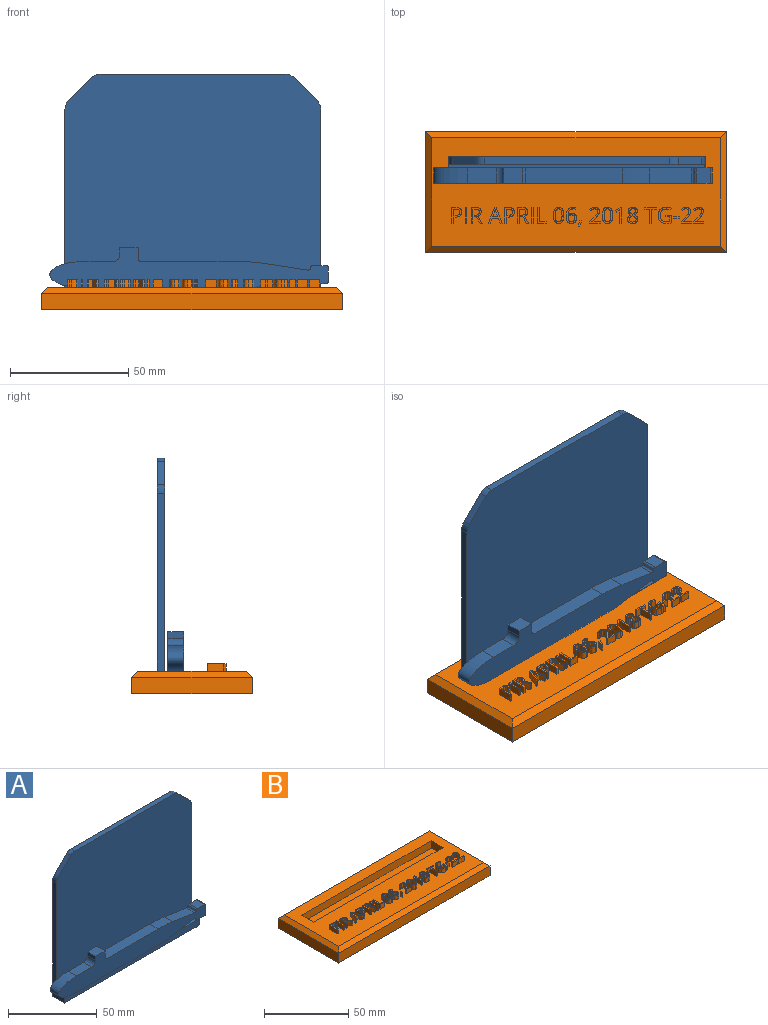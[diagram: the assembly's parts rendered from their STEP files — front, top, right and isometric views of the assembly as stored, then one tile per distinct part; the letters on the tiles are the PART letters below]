
ASSEMBLY  parts=2 mates=1
PART A: 43 faces, bbox 117.5x11x95.3 mm
  f0: plane 70.92x1.52mm, normal (0,0,-1), area 108.1mm2, adj f1,f13,f15,f32
  f1: plane 23.61x6.6mm, normal (0.15,0,-0.99), area 157.8mm2, adj f0,f14,f15,f18,f25
  f2: plane 6.6x0.11mm, normal (-1,0,0), area 0.7mm2, adj f14,f15,f18,f19
  f3: plane 6.6x5.84mm, normal (0,0,-1), area 38.6mm2, adj f14,f15,f19,f20
  f4: plane 6.6x5.84mm, normal (1,0,0), area 38.6mm2, adj f14,f15,f20,f21
  f5: plane 6.6x5.84mm, normal (0,0,1), area 38.6mm2, adj f14,f15,f21,f22
  f6: plane 6.6x0.11mm, normal (-1,0,0), area 0.7mm2, adj f14,f15,f22,f23
  f7: plane 17.86x6.6mm, normal (0.15,0,0.99), area 119.4mm2, adj f14,f15,f23,f24
  f8: plane 40.71x6.6mm, normal (0,0,1), area 268.9mm2, adj f14,f15,f17,f24
  f9: plane 6.6x4.36mm, normal (1,0,0), area 28.8mm2, adj f10,f14,f15,f17
  f10: plane 7.62x6.6mm, normal (0,0,1), area 50.3mm2, adj f9,f11,f14,f15
  f11: plane 6.6x2.84mm, normal (-1,0,0), area 18.7mm2, adj f10,f14,f15,f16
  f12: plane 12.19x6.6mm, normal (0,0,1), area 80.5mm2, adj f13,f14,f15,f16
  f13: extruded ~14.34x11.13mm, area 216.7mm2, adj f0,f12,f14,f15,f25
  f14: plane 117.52x17.01mm, normal (0,1,0), area 1199.5mm2, adj f1,f2,f3,f4,f5,f6,f7,f8
  f15: plane 117.52x17.01mm, normal (0,-1,0), area 1199.5mm2, adj f0,f1,f2,f3,f4,f5,f6,f7
  f16: cylinder r=3.05mm len=6.6mm, axis (0,1,0), area 31.6mm2, adj f11,f12,f14,f15
  f17: cylinder r=1.52mm len=6.6mm, axis (0,-1,0), area 15.8mm2, adj f8,f9,f14,f15
  f18: cylinder r=0.89mm len=6.6mm, axis (0,1,0), area 10.1mm2, adj f1,f2,f14,f15
  f19: cylinder r=0.89mm len=6.6mm, axis (0,-1,0), area 9.2mm2, adj f2,f3,f14,f15
  f20: cylinder r=0.89mm len=6.6mm, axis (0,1,0), area 9.2mm2, adj f3,f4,f14,f15
  f21: cylinder r=0.89mm len=6.6mm, axis (0,-1,0), area 9.2mm2, adj f4,f5,f14,f15
  f22: cylinder r=0.89mm len=6.6mm, axis (0,1,0), area 9.2mm2, adj f5,f6,f14,f15
  f23: cylinder r=0.89mm len=6.6mm, axis (0,-1,0), area 10.1mm2, adj f6,f7,f14,f15
  f24: cylinder r=76.2mm len=11.57mm, axis (0,-1,0), area 76.7mm2, adj f7,f8,f14,f15
  f25: plane 107.95x6.35mm, normal (0,0,1), area 325.2mm2, adj f1,f13,f14,f26,f27,f29,f32
  f26: plane 107.95x90.17mm, normal (0,-1,0), area 9570.3mm2, adj f25,f27,f29,f30,f33,f34,f35,f36
  f27: plane 79.68x9.53mm, normal (-1,0,0), area 280.4mm2, adj f25,f26,f31,f32,f35,f40
  f28: plane 106.43x8mm, normal (0,0,-1), area 851.5mm2, adj f39,f40,f41,f42
  f29: plane 79.68x9.53mm, normal (1,0,0), area 280.4mm2, adj f25,f26,f31,f32,f36,f41
  f30: plane 78.34x3.18mm, normal (0,0,1), area 248.7mm2, adj f26,f31,f37,f38
  f31: plane 107.95x94.49mm, normal (0,1,0), area 10036.5mm2, adj f27,f29,f30,f33,f34,f35,f36,f37
  f32: plane 107.95x4.32mm, normal (0,-1,0), area 466.1mm2, adj f0,f25,f27,f29,f42
  f33: plane 9.72x9.72mm, normal (0.71,0,0.71), area 43.7mm2, adj f26,f31,f36,f37
  f34: plane 9.72x9.72mm, normal (-0.71,0,0.71), area 43.7mm2, adj f26,f31,f35,f38
  f35: cylinder r=5.08mm len=3.59mm, axis (0,-1,0), area 12.7mm2, adj f26,f27,f31,f34
  f36: cylinder r=5.08mm len=3.59mm, axis (0,1,0), area 12.7mm2, adj f26,f29,f31,f33
  f37: cylinder r=5.08mm len=3.59mm, axis (0,1,0), area 12.7mm2, adj f26,f30,f31,f33
  f38: cylinder r=5.08mm len=3.59mm, axis (0,1,0), area 12.7mm2, adj f26,f30,f31,f34
  f39: plane 107.95x0.76mm, normal (0,0.71,-0.71), area 115.5mm2, adj f28,f31,f40,f41
  f40: plane 9.53x0.76mm, normal (-0.71,0,-0.71), area 9.4mm2, adj f27,f28,f39,f42
  f41: plane 9.53x0.76mm, normal (0.71,0,-0.71), area 9.4mm2, adj f28,f29,f39,f42
  f42: plane 107.95x0.76mm, normal (0,-0.71,-0.71), area 115.5mm2, adj f28,f32,f40,f41
PART B: 334 faces, bbox 127x50.8x12.7 mm
  f0: plane 121.92x45.72mm, normal (0,0,1), area 4230.8mm2, adj f6,f7,f8,f9,f16,f17,f18,f19
  f1: plane 50.8x6.99mm, normal (-1,0,0), area 354.8mm2, adj f2,f4,f5,f9
  f2: plane 127x50.8mm, normal (0,0,-1), area 6451.6mm2, adj f1,f3,f4,f5
  f3: plane 50.8x6.99mm, normal (1,0,0), area 354.8mm2, adj f2,f4,f5,f6
  f4: plane 127x6.99mm, normal (0,-1,0), area 887.1mm2, adj f1,f2,f3,f7
  f5: plane 127x6.99mm, normal (0,1,0), area 887.1mm2, adj f1,f2,f3,f8
  f6: plane 50.8x2.54mm, normal (0.71,0,0.71), area 173.4mm2, adj f0,f3,f7,f8
  f7: plane 127x2.54mm, normal (0,-0.71,0.71), area 447.1mm2, adj f0,f4,f6,f9
  f8: plane 127x2.54mm, normal (0,0.71,0.71), area 447.1mm2, adj f0,f5,f6,f9
  f9: plane 50.8x2.54mm, normal (-0.71,0,0.71), area 173.4mm2, adj f0,f1,f7,f8
  f10: plane 3.18x0.7mm, normal (0,1,0), area 2.2mm2, adj f11,f24,f25,f26
  f11: plane 3.18x2.69mm, normal (1,0,0), area 8.6mm2, adj f10,f12,f25,f26
  f12: plane 3.18x0.86mm, normal (0,-1,0), area 2.7mm2, adj f11,f13,f25,f26
  f13: extruded ~3.18x1.34mm, area 4.5mm2, adj f12,f14,f25,f26
  f14: extruded ~3.18x0.98mm, area 3.5mm2, adj f13,f15,f25,f26
  f15: extruded ~3.18x1.06mm, area 3.8mm2, adj f14,f24,f25,f26
  f16: extruded ~3.18x1.55mm, area 5.6mm2, adj f0,f17,f23,f25
  f17: extruded ~3.18x2.48mm, area 11.4mm2, adj f0,f16,f18,f25
  f18: plane 3.18x1.72mm, normal (0,1,0), area 5.5mm2, adj f0,f17,f19,f25
  f19: plane 6.63x3.18mm, normal (-1,0,0), area 21.1mm2, adj f0,f18,f20,f25
  f20: plane 3.18x0.77mm, normal (0,-1,0), area 2.4mm2, adj f0,f19,f21,f25
  f21: plane 3.18x2.61mm, normal (1,0,0), area 8.3mm2, adj f0,f20,f22,f25
  f22: plane 3.18x0.78mm, normal (0,-1,0), area 2.5mm2, adj f0,f21,f23,f25
  f23: extruded ~3.18x1.97mm, area 6.6mm2, adj f0,f16,f22,f25
  f24: extruded ~3.18x1.48mm, area 4.9mm2, adj f10,f15,f25,f26
  f25: plane 6.63x4.2mm, normal (0,0,1), area 10.8mm2, adj f10,f11,f12,f13,f14,f15,f16,f17
  f26: plane 2.69x2.64mm, normal (0,0,1), area 6.3mm2, adj f10,f11,f12,f13,f14,f15,f24
  f27: plane 6.63x3.18mm, normal (-1,0,0), area 21.1mm2, adj f0,f28,f30,f31
  f28: plane 3.18x0.77mm, normal (0,-1,0), area 2.4mm2, adj f0,f27,f29,f31
  f29: plane 6.63x3.18mm, normal (1,0,0), area 21.1mm2, adj f0,f28,f30,f31
  f30: plane 3.18x0.77mm, normal (0,1,0), area 2.4mm2, adj f0,f27,f29,f31
  f31: plane 6.63x0.77mm, normal (0,0,1), area 5.1mm2, adj f27,f28,f29,f30
  f32: plane 3.18x1.06mm, normal (0,1,0), area 3.4mm2, adj f33,f49,f50,f51
  f33: plane 3.18x2.54mm, normal (1,0,0), area 8mm2, adj f32,f34,f50,f51
  f34: plane 3.18x1mm, normal (0,-1,0), area 3.2mm2, adj f33,f35,f50,f51
  f35: extruded ~3.18x1.25mm, area 4.1mm2, adj f34,f36,f50,f51
  f36: extruded ~3.18x0.95mm, area 3.4mm2, adj f35,f37,f50,f51
  f37: extruded ~3.18x0.97mm, area 3.4mm2, adj f36,f49,f50,f51
  f38: plane 3.18x2.76mm, normal (1,0,0), area 8.8mm2, adj f0,f39,f48,f50
  f39: plane 3.18x1.38mm, normal (0,-1,0), area 4.4mm2, adj f0,f38,f40,f50
  f40: plane 3.18x2.76mm, normal (-0.86,-0.5,0), area 10.1mm2, adj f0,f39,f41,f50
  f41: plane 3.18x0.91mm, normal (0,-1,0), area 2.9mm2, adj f0,f40,f42,f50
  f42: plane 3.18x2.98mm, normal (0.86,0.52,0), area 11.1mm2, adj f0,f41,f43,f50
  f43: extruded ~3.18x1.78mm, area 7.6mm2, adj f0,f42,f44,f50
  f44: extruded ~3.18x1.41mm, area 5mm2, adj f0,f43,f45,f50
  f45: extruded ~3.18x1.8mm, area 6mm2, adj f0,f44,f46,f50
  f46: plane 3.18x1.82mm, normal (0,1,0), area 5.8mm2, adj f0,f45,f47,f50
  f47: plane 6.63x3.18mm, normal (-1,0,0), area 21.1mm2, adj f0,f46,f48,f50
  f48: plane 3.18x0.77mm, normal (0,-1,0), area 2.4mm2, adj f0,f38,f47,f50
  f49: extruded ~3.18x1.2mm, area 4mm2, adj f32,f37,f50,f51
  f50: plane 6.63x4.67mm, normal (0,0,1), area 13.2mm2, adj f32,f33,f34,f35,f36,f37,f38,f39
  f51: plane 2.64x2.54mm, normal (0,0,1), area 6mm2, adj f32,f33,f34,f35,f36,f37,f49
  f52: plane 3.18x2.06mm, normal (-0.94,-0.35,0), area 7mm2, adj f53,f64,f65,f66
  f53: plane 3.18x2.15mm, normal (0,1,0), area 6.8mm2, adj f52,f54,f65,f66
  f54: plane 3.18x2.06mm, normal (0.94,-0.35,0), area 7mm2, adj f53,f55,f65,f66
  f55: extruded ~3.18x0.96mm, area 3.2mm2, adj f54,f64,f65,f66
  f56: plane 3.18x2.11mm, normal (-0.93,-0.36,0), area 7.2mm2, adj f0,f57,f63,f65
  f57: plane 3.18x0.8mm, normal (0,-1,0), area 2.5mm2, adj f0,f56,f58,f65
  f58: plane 6.66x3.18mm, normal (0.93,0.36,0), area 22.7mm2, adj f0,f57,f59,f65
  f59: plane 3.18x0.65mm, normal (0,1,0), area 2.1mm2, adj f0,f58,f60,f65
  f60: plane 6.66x3.18mm, normal (-0.93,0.37,0), area 22.7mm2, adj f0,f59,f61,f65
  f61: plane 3.18x0.78mm, normal (0,-1,0), area 2.5mm2, adj f0,f60,f62,f65
  f62: plane 3.18x2.11mm, normal (0.93,-0.36,0), area 7.2mm2, adj f0,f61,f63,f65
  f63: plane 3.18x2.66mm, normal (0,-1,0), area 8.4mm2, adj f0,f56,f62,f65
  f64: extruded ~3.18x0.96mm, area 3.2mm2, adj f52,f55,f65,f66
  f65: plane 6.66x5.88mm, normal (0,0,1), area 11.3mm2, adj f52,f53,f54,f55,f56,f57,f58,f59
  f66: plane 3.01x2.15mm, normal (0,0,1), area 3.1mm2, adj f52,f53,f54,f55,f64
  f67: plane 3.18x0.7mm, normal (0,1,0), area 2.2mm2, adj f68,f81,f82,f83
  f68: plane 3.18x2.69mm, normal (1,0,0), area 8.6mm2, adj f67,f69,f82,f83
  f69: plane 3.18x0.86mm, normal (0,-1,0), area 2.7mm2, adj f68,f70,f82,f83
  f70: extruded ~3.18x1.34mm, area 4.5mm2, adj f69,f71,f82,f83
  f71: extruded ~3.18x0.98mm, area 3.5mm2, adj f70,f72,f82,f83
  f72: extruded ~3.18x1.06mm, area 3.8mm2, adj f71,f81,f82,f83
  f73: extruded ~3.18x1.55mm, area 5.6mm2, adj f0,f74,f80,f82
  f74: extruded ~3.18x2.48mm, area 11.4mm2, adj f0,f73,f75,f82
  f75: plane 3.18x1.72mm, normal (0,1,0), area 5.5mm2, adj f0,f74,f76,f82
  f76: plane 6.63x3.18mm, normal (-1,0,0), area 21.1mm2, adj f0,f75,f77,f82
  f77: plane 3.18x0.77mm, normal (0,-1,0), area 2.4mm2, adj f0,f76,f78,f82
  f78: plane 3.18x2.61mm, normal (1,0,0), area 8.3mm2, adj f0,f77,f79,f82
  f79: plane 3.18x0.78mm, normal (0,-1,0), area 2.5mm2, adj f0,f78,f80,f82
  f80: extruded ~3.18x1.97mm, area 6.6mm2, adj f0,f73,f79,f82
  f81: extruded ~3.18x1.48mm, area 4.9mm2, adj f67,f72,f82,f83
  f82: plane 6.63x4.2mm, normal (0,0,1), area 10.8mm2, adj f67,f68,f69,f70,f71,f72,f73,f74
  f83: plane 2.69x2.64mm, normal (0,0,1), area 6.3mm2, adj f67,f68,f69,f70,f71,f72,f81
  f84: plane 3.18x1.06mm, normal (0,1,0), area 3.4mm2, adj f85,f101,f102,f103
  f85: plane 3.18x2.54mm, normal (1,0,0), area 8mm2, adj f84,f86,f102,f103
  f86: plane 3.18x1mm, normal (0,-1,0), area 3.2mm2, adj f85,f87,f102,f103
  f87: extruded ~3.18x1.25mm, area 4.1mm2, adj f86,f88,f102,f103
  f88: extruded ~3.18x0.95mm, area 3.4mm2, adj f87,f89,f102,f103
  f89: extruded ~3.18x0.97mm, area 3.4mm2, adj f88,f101,f102,f103
  f90: plane 3.18x2.76mm, normal (1,0,0), area 8.8mm2, adj f0,f91,f100,f102
  f91: plane 3.18x1.38mm, normal (0,-1,0), area 4.4mm2, adj f0,f90,f92,f102
  f92: plane 3.18x2.76mm, normal (-0.86,-0.5,0), area 10.1mm2, adj f0,f91,f93,f102
  f93: plane 3.18x0.91mm, normal (0,-1,0), area 2.9mm2, adj f0,f92,f94,f102
  f94: plane 3.18x2.98mm, normal (0.86,0.52,0), area 11.1mm2, adj f0,f93,f95,f102
  f95: extruded ~3.18x1.78mm, area 7.6mm2, adj f0,f94,f96,f102
  f96: extruded ~3.18x1.41mm, area 5mm2, adj f0,f95,f97,f102
  f97: extruded ~3.18x1.8mm, area 6mm2, adj f0,f96,f98,f102
  f98: plane 3.18x1.82mm, normal (0,1,0), area 5.8mm2, adj f0,f97,f99,f102
  f99: plane 6.63x3.18mm, normal (-1,0,0), area 21.1mm2, adj f0,f98,f100,f102
  f100: plane 3.18x0.77mm, normal (0,-1,0), area 2.4mm2, adj f0,f90,f99,f102
  f101: extruded ~3.18x1.2mm, area 4mm2, adj f84,f89,f102,f103
  f102: plane 6.63x4.67mm, normal (0,0,1), area 13.2mm2, adj f84,f85,f86,f87,f88,f89,f90,f91
  f103: plane 2.64x2.54mm, normal (0,0,1), area 6mm2, adj f84,f85,f86,f87,f88,f89,f101
  f104: plane 6.63x3.18mm, normal (-1,0,0), area 21.1mm2, adj f0,f105,f107,f108
  f105: plane 3.18x0.77mm, normal (0,-1,0), area 2.4mm2, adj f0,f104,f106,f108
  f106: plane 6.63x3.18mm, normal (1,0,0), area 21.1mm2, adj f0,f105,f107,f108
  f107: plane 3.18x0.77mm, normal (0,1,0), area 2.4mm2, adj f0,f104,f106,f108
  f108: plane 6.63x0.77mm, normal (0,0,1), area 5.1mm2, adj f104,f105,f106,f107
  f109: plane 6.63x3.18mm, normal (-1,0,0), area 21.1mm2, adj f0,f110,f114,f115
  f110: plane 3.7x3.18mm, normal (0,-1,0), area 11.7mm2, adj f0,f109,f111,f115
  f111: plane 3.18x0.7mm, normal (1,0,0), area 2.2mm2, adj f0,f110,f112,f115
  f112: plane 3.18x2.93mm, normal (0,1,0), area 9.3mm2, adj f0,f111,f113,f115
  f113: plane 5.93x3.18mm, normal (1,0,0), area 18.8mm2, adj f0,f112,f114,f115
  f114: plane 3.18x0.77mm, normal (0,1,0), area 2.4mm2, adj f0,f109,f113,f115
  f115: plane 6.63x3.7mm, normal (0,0,1), area 7.2mm2, adj f109,f110,f111,f112,f113,f114
  f116: extruded ~3.18x2.11mm, area 6.8mm2, adj f117,f131,f132,f133
  f117: extruded ~3.18x2.1mm, area 6.8mm2, adj f116,f118,f132,f133
  f118: extruded ~3.18x1.08mm, area 4.3mm2, adj f117,f119,f132,f133
  f119: extruded ~3.18x1.09mm, area 4.3mm2, adj f118,f120,f132,f133
  f120: extruded ~3.18x2.09mm, area 6.8mm2, adj f119,f121,f132,f133
  f121: extruded ~3.18x2.1mm, area 6.8mm2, adj f120,f122,f132,f133
  f122: extruded ~3.18x1.09mm, area 4.3mm2, adj f121,f131,f132,f133
  f123: extruded ~3.18x2.57mm, area 8.4mm2, adj f0,f124,f130,f132
  f124: extruded ~3.18x2.53mm, area 8.3mm2, adj f0,f123,f125,f132
  f125: extruded ~3.18x1.64mm, area 6.2mm2, adj f0,f124,f126,f132
  f126: extruded ~3.18x1.65mm, area 6.1mm2, adj f0,f125,f127,f132
  f127: extruded ~3.18x2.57mm, area 8.4mm2, adj f0,f126,f128,f132
  f128: extruded ~3.18x2.55mm, area 8.4mm2, adj f0,f127,f129,f132
  f129: extruded ~3.18x1.63mm, area 6.1mm2, adj f0,f128,f130,f132
  f130: extruded ~3.18x1.66mm, area 6.2mm2, adj f0,f123,f129,f132
  f131: extruded ~3.18x1.08mm, area 4.3mm2, adj f116,f122,f132,f133
  f132: plane 6.83x4.39mm, normal (0,0,1), area 11.6mm2, adj f116,f117,f118,f119,f120,f121,f122,f123
  f133: plane 5.53x2.85mm, normal (0,0,1), area 13.3mm2, adj f116,f117,f118,f119,f120,f121,f122,f131
  f134: extruded ~3.18x1mm, area 3.5mm2, adj f135,f158,f159,f160
  f135: extruded ~3.18x0.76mm, area 2.6mm2, adj f134,f136,f159,f160
  f136: extruded ~3.18x0.64mm, area 2.6mm2, adj f135,f137,f159,f160
  f137: extruded ~3.18x0.87mm, area 2.8mm2, adj f136,f138,f159,f160
  f138: extruded ~3.18x0.61mm, area 2.1mm2, adj f137,f139,f159,f160
  f139: extruded ~3.18x0.54mm, area 2.3mm2, adj f138,f140,f159,f160
  f140: extruded ~3.18x0.75mm, area 2.5mm2, adj f139,f141,f159,f160
  f141: extruded ~3.18x0.99mm, area 3.5mm2, adj f140,f142,f159,f160
  f142: extruded ~3.18x1.03mm, area 3.5mm2, adj f141,f158,f159,f160
  f143: extruded ~3.18x2.92mm, area 9.8mm2, adj f0,f144,f157,f159
  f144: extruded ~3.18x2.15mm, area 7.2mm2, adj f0,f143,f145,f159
  f145: extruded ~3.18x1.63mm, area 6mm2, adj f0,f144,f146,f159
  f146: extruded ~3.18x1.53mm, area 5.4mm2, adj f0,f145,f147,f159
  f147: extruded ~3.18x1.63mm, area 5.6mm2, adj f0,f146,f148,f159
  f148: extruded ~3.18x1.46mm, area 5.1mm2, adj f0,f147,f149,f159
  f149: extruded ~3.18x1.41mm, area 4.9mm2, adj f0,f148,f150,f159
  f150: extruded ~3.18x1.58mm, area 5.9mm2, adj f0,f149,f151,f159
  f151: plane 3.18x0.05mm, normal (0,1,0), area 0.2mm2, adj f0,f150,f152,f159
  f152: extruded ~3.18x2.09mm, area 7mm2, adj f0,f151,f153,f159
  f153: extruded ~3.18x1.63mm, area 5.8mm2, adj f0,f152,f154,f159
  f154: extruded ~3.18x0.8mm, area 2.6mm2, adj f0,f153,f155,f159
  f155: plane 3.18x0.65mm, normal (1,0,0), area 2.1mm2, adj f0,f154,f156,f159
  f156: extruded ~3.18x0.81mm, area 2.6mm2, adj f0,f155,f157,f159
  f157: extruded ~3.18x2.25mm, area 8.1mm2, adj f0,f143,f156,f159
  f158: extruded ~3.18x1.17mm, area 4mm2, adj f134,f142,f159,f160
  f159: plane 6.82x4.33mm, normal (0,0,1), area 11.4mm2, adj f134,f135,f136,f137,f138,f139,f140,f141
  f160: plane 2.99x2.81mm, normal (0,0,1), area 6.8mm2, adj f134,f135,f136,f137,f138,f139,f140,f141
  f161: plane 3.18x0.1mm, normal (0.84,0.55,0), area 0.4mm2, adj f0,f162,f167,f168
  f162: plane 3.18x0.83mm, normal (0,1,0), area 2.6mm2, adj f0,f161,f163,f168
  f163: extruded ~3.18x1.11mm, area 3.6mm2, adj f0,f162,f164,f168
  f164: extruded ~3.18x1.17mm, area 3.8mm2, adj f0,f163,f165,f168
  f165: plane 3.18x0.57mm, normal (0,-1,0), area 1.8mm2, adj f0,f164,f166,f168
  f166: extruded ~3.18x1.12mm, area 3.8mm2, adj f0,f165,f167,f168
  f167: extruded ~3.18x1.06mm, area 3.5mm2, adj f0,f161,f166,f168
  f168: plane 2.28x1.37mm, normal (0,0,1), area 1.7mm2, adj f161,f162,f163,f164,f165,f166,f167
  f169: plane 4.36x3.18mm, normal (0,-1,0), area 13.8mm2, adj f0,f170,f188,f189
  f170: plane 3.18x0.7mm, normal (1,0,0), area 2.2mm2, adj f0,f169,f171,f189
  f171: plane 3.41x3.18mm, normal (0,1,0), area 10.8mm2, adj f0,f170,f172,f189
  f172: plane 3.18x0.04mm, normal (1,0,0), area 0.1mm2, adj f0,f171,f173,f189
  f173: plane 3.18x1.45mm, normal (0.7,-0.71,0), area 6.4mm2, adj f0,f172,f174,f189
  f174: extruded ~3.18x1.56mm, area 6.5mm2, adj f0,f173,f175,f189
  f175: extruded ~3.18x1.25mm, area 4.2mm2, adj f0,f174,f176,f189
  f176: extruded ~3.18x1.29mm, area 4.6mm2, adj f0,f175,f177,f189
  f177: extruded ~3.18x1.47mm, area 5mm2, adj f0,f176,f178,f189
  f178: extruded ~3.18x2mm, area 6.9mm2, adj f0,f177,f179,f189
  f179: plane 3.18x0.51mm, normal (-0.79,-0.61,0), area 2.1mm2, adj f0,f178,f180,f189
  f180: extruded ~3.18x0.82mm, area 3.1mm2, adj f0,f179,f181,f189
  f181: extruded ~3.18x0.78mm, area 2.5mm2, adj f0,f180,f182,f189
  f182: extruded ~3.18x0.89mm, area 3.1mm2, adj f0,f181,f183,f189
  f183: extruded ~3.18x0.84mm, area 2.9mm2, adj f0,f182,f184,f189
  f184: extruded ~3.18x0.7mm, area 2.3mm2, adj f0,f183,f185,f189
  f185: extruded ~3.18x0.67mm, area 2.5mm2, adj f0,f184,f186,f189
  f186: extruded ~3.18x1.15mm, area 5mm2, adj f0,f185,f187,f189
  f187: plane 3.18x1.75mm, normal (-0.71,0.71,0), area 7.9mm2, adj f0,f186,f188,f189
  f188: plane 3.18x0.65mm, normal (-1,0,0), area 2.1mm2, adj f0,f169,f187,f189
  f189: plane 6.73x4.36mm, normal (0,0,1), area 9.7mm2, adj f169,f170,f171,f172,f173,f174,f175,f176
  f190: extruded ~3.18x2.11mm, area 6.8mm2, adj f191,f205,f206,f207
  f191: extruded ~3.18x2.1mm, area 6.8mm2, adj f190,f192,f206,f207
  f192: extruded ~3.18x1.08mm, area 4.3mm2, adj f191,f193,f206,f207
  f193: extruded ~3.18x1.09mm, area 4.3mm2, adj f192,f194,f206,f207
  f194: extruded ~3.18x2.09mm, area 6.8mm2, adj f193,f195,f206,f207
  f195: extruded ~3.18x2.1mm, area 6.8mm2, adj f194,f196,f206,f207
  f196: extruded ~3.18x1.09mm, area 4.3mm2, adj f195,f205,f206,f207
  f197: extruded ~3.18x2.57mm, area 8.4mm2, adj f0,f198,f204,f206
  f198: extruded ~3.18x2.53mm, area 8.3mm2, adj f0,f197,f199,f206
  f199: extruded ~3.18x1.64mm, area 6.2mm2, adj f0,f198,f200,f206
  f200: extruded ~3.18x1.65mm, area 6.1mm2, adj f0,f199,f201,f206
  f201: extruded ~3.18x2.57mm, area 8.4mm2, adj f0,f200,f202,f206
  f202: extruded ~3.18x2.55mm, area 8.4mm2, adj f0,f201,f203,f206
  f203: extruded ~3.18x1.63mm, area 6.1mm2, adj f0,f202,f204,f206
  f204: extruded ~3.18x1.66mm, area 6.2mm2, adj f0,f197,f203,f206
  f205: extruded ~3.18x1.08mm, area 4.3mm2, adj f190,f196,f206,f207
  f206: plane 6.83x4.39mm, normal (0,0,1), area 11.6mm2, adj f190,f191,f192,f193,f194,f195,f196,f197
  f207: plane 5.53x2.85mm, normal (0,0,1), area 13.3mm2, adj f190,f191,f192,f193,f194,f195,f196,f205
  f208: plane 3.18x0.73mm, normal (0,-1,0), area 2.3mm2, adj f0,f209,f216,f217
  f209: plane 6.63x3.18mm, normal (1,0,0), area 21.1mm2, adj f0,f208,f210,f217
  f210: plane 3.18x0.63mm, normal (0,1,0), area 2mm2, adj f0,f209,f211,f217
  f211: plane 3.18x1.75mm, normal (-0.61,0.79,0), area 7mm2, adj f0,f210,f212,f217
  f212: plane 3.18x0.52mm, normal (-0.79,-0.61,0), area 2.1mm2, adj f0,f211,f213,f217
  f213: extruded ~3.18x1.08mm, area 4.4mm2, adj f0,f212,f214,f217
  f214: extruded ~3.18x0.21mm, area 0.9mm2, adj f0,f213,f215,f217
  f215: extruded ~3.18x1.12mm, area 3.5mm2, adj f0,f214,f216,f217
  f216: plane 4.73x3.18mm, normal (-1,0,0), area 15mm2, adj f0,f208,f215,f217
  f217: plane 6.63x2.39mm, normal (0,0,1), area 6mm2, adj f208,f209,f210,f211,f212,f213,f214,f215
  f218: extruded ~3.18x0.89mm, area 3mm2, adj f219,f248,f249,f250
  f219: extruded ~3.18x0.91mm, area 3.1mm2, adj f218,f220,f249,f250
  f220: extruded ~3.18x0.73mm, area 2.6mm2, adj f219,f221,f249,f250
  f221: extruded ~3.18x0.73mm, area 2.5mm2, adj f220,f222,f249,f250
  f222: extruded ~3.18x0.92mm, area 3.5mm2, adj f221,f223,f249,f250
  f223: extruded ~3.18x0.99mm, area 3.7mm2, adj f222,f224,f249,f250
  f224: extruded ~3.18x0.72mm, area 2.5mm2, adj f223,f248,f249,f250
  f225: extruded ~3.18x0.85mm, area 3.1mm2, adj f226,f246,f249,f251
  f226: extruded ~3.18x0.84mm, area 2.9mm2, adj f225,f227,f249,f251
  f227: extruded ~3.18x0.98mm, area 3.7mm2, adj f226,f228,f249,f251
  f228: extruded ~3.18x1.23mm, area 4.5mm2, adj f227,f229,f249,f251
  f229: extruded ~3.18x0.78mm, area 2.8mm2, adj f228,f230,f249,f251
  f230: extruded ~3.18x0.87mm, area 3.1mm2, adj f229,f231,f249,f251
  f231: extruded ~3.18x1.05mm, area 3.6mm2, adj f230,f246,f249,f251
  f232: extruded ~3.18x1.44mm, area 4.8mm2, adj f0,f233,f247,f249
  f233: extruded ~3.18x1.43mm, area 4.8mm2, adj f0,f232,f234,f249
  f234: extruded ~3.18x1.15mm, area 4.2mm2, adj f0,f233,f235,f249
  f235: extruded ~3.18x0.92mm, area 3.1mm2, adj f0,f234,f236,f249
  f236: extruded ~3.18x0.9mm, area 3.8mm2, adj f0,f235,f237,f249
  f237: extruded ~3.18x1.77mm, area 7.6mm2, adj f0,f236,f238,f249
  f238: extruded ~3.18x1.32mm, area 4.7mm2, adj f0,f237,f239,f249
  f239: extruded ~3.18x1.63mm, area 5.5mm2, adj f0,f238,f240,f249
  f240: extruded ~3.18x1.58mm, area 5.4mm2, adj f0,f239,f241,f249
  f241: extruded ~3.18x1.32mm, area 4.7mm2, adj f0,f240,f242,f249
  f242: extruded ~3.18x0.98mm, area 3.4mm2, adj f0,f241,f243,f249
  f243: extruded ~3.18x1.15mm, area 4.5mm2, adj f0,f242,f244,f249
  f244: extruded ~3.18x0.97mm, area 3.9mm2, adj f0,f243,f245,f249
  f245: extruded ~3.18x0.89mm, area 3.1mm2, adj f0,f244,f247,f249
  f246: extruded ~3.18x1.06mm, area 3.6mm2, adj f225,f231,f249,f251
  f247: extruded ~3.18x1.16mm, area 4.2mm2, adj f0,f232,f245,f249
  f248: extruded ~3.18x0.73mm, area 2.6mm2, adj f218,f224,f249,f250
  f249: plane 6.82x4.36mm, normal (0,0,1), area 13mm2, adj f218,f219,f220,f221,f222,f223,f224,f225
  f250: plane 2.45x2.31mm, normal (0,0,1), area 4.3mm2, adj f218,f219,f220,f221,f222,f223,f224,f248
  f251: plane 2.87x2.64mm, normal (0,0,1), area 5.8mm2, adj f225,f226,f227,f228,f229,f230,f231,f246
  f252: plane 3.18x0.77mm, normal (0,-1,0), area 2.4mm2, adj f0,f253,f259,f260
  f253: plane 5.95x3.18mm, normal (1,0,0), area 18.9mm2, adj f0,f252,f254,f260
  f254: plane 3.18x2.1mm, normal (0,-1,0), area 6.7mm2, adj f0,f253,f255,f260
  f255: plane 3.18x0.69mm, normal (1,0,0), area 2.2mm2, adj f0,f254,f256,f260
  f256: plane 4.97x3.18mm, normal (0,1,0), area 15.8mm2, adj f0,f255,f257,f260
  f257: plane 3.18x0.69mm, normal (-1,0,0), area 2.2mm2, adj f0,f256,f258,f260
  f258: plane 3.18x2.1mm, normal (0,-1,0), area 6.7mm2, adj f0,f257,f259,f260
  f259: plane 5.95x3.18mm, normal (-1,0,0), area 18.9mm2, adj f0,f252,f258,f260
  f260: plane 6.63x4.97mm, normal (0,0,1), area 8mm2, adj f252,f253,f254,f255,f256,f257,f258,f259
  f261: plane 3.18x2.25mm, normal (0,1,0), area 7.2mm2, adj f0,f262,f280,f281
  f262: plane 3.18x0.69mm, normal (-1,0,0), area 2.2mm2, adj f0,f261,f263,f281
  f263: plane 3.18x1.48mm, normal (0,-1,0), area 4.7mm2, adj f0,f262,f264,f281
  f264: plane 3.18x2.04mm, normal (-1,0,0), area 6.5mm2, adj f0,f263,f265,f281
  f265: extruded ~3.18x1.35mm, area 4.3mm2, adj f0,f264,f266,f281
  f266: extruded ~3.18x1.93mm, area 6.7mm2, adj f0,f265,f267,f281
  f267: extruded ~3.18x2.04mm, area 7mm2, adj f0,f266,f268,f281
  f268: extruded ~3.18x2mm, area 6.9mm2, adj f0,f267,f269,f281
  f269: extruded ~3.18x1.89mm, area 6.6mm2, adj f0,f268,f270,f281
  f270: extruded ~3.18x1.73mm, area 5.7mm2, adj f0,f269,f271,f281
  f271: plane 3.18x0.68mm, normal (0.92,-0.4,0), area 2.4mm2, adj f0,f270,f272,f281
  f272: extruded ~3.18x1.98mm, area 6.4mm2, adj f0,f271,f273,f281
  f273: extruded ~3.18x1.83mm, area 6mm2, adj f0,f272,f274,f281
  f274: extruded ~3.18x1.2mm, area 5.4mm2, adj f0,f273,f275,f281
  f275: extruded ~3.18x1.81mm, area 6mm2, adj f0,f274,f276,f281
  f276: extruded ~3.18x2.51mm, area 8.6mm2, adj f0,f275,f277,f281
  f277: extruded ~3.18x2.34mm, area 8.2mm2, adj f0,f276,f278,f281
  f278: extruded ~3.18x1.26mm, area 4mm2, adj f0,f277,f279,f281
  f279: extruded ~3.18x1.07mm, area 3.5mm2, adj f0,f278,f280,f281
  f280: plane 3.22x3.18mm, normal (1,0,0), area 10.2mm2, adj f0,f261,f279,f281
  f281: plane 6.82x5.52mm, normal (0,0,1), area 13.3mm2, adj f261,f262,f263,f264,f265,f266,f267,f268
  f282: plane 3.18x0.69mm, normal (-1,0,0), area 2.2mm2, adj f0,f283,f285,f286
  f283: plane 3.18x2.23mm, normal (0,-1,0), area 7.1mm2, adj f0,f282,f284,f286
  f284: plane 3.18x0.69mm, normal (1,0,0), area 2.2mm2, adj f0,f283,f285,f286
  f285: plane 3.18x2.23mm, normal (0,1,0), area 7.1mm2, adj f0,f282,f284,f286
  f286: plane 2.23x0.69mm, normal (0,0,1), area 1.5mm2, adj f282,f283,f284,f285
  f287: plane 4.36x3.18mm, normal (0,-1,0), area 13.8mm2, adj f0,f288,f306,f307
  f288: plane 3.18x0.7mm, normal (1,0,0), area 2.2mm2, adj f0,f287,f289,f307
  f289: plane 3.41x3.18mm, normal (0,1,0), area 10.8mm2, adj f0,f288,f290,f307
  f290: plane 3.18x0.04mm, normal (1,0,0), area 0.1mm2, adj f0,f289,f291,f307
  f291: plane 3.18x1.45mm, normal (0.7,-0.71,0), area 6.4mm2, adj f0,f290,f292,f307
  f292: extruded ~3.18x1.56mm, area 6.5mm2, adj f0,f291,f293,f307
  f293: extruded ~3.18x1.25mm, area 4.2mm2, adj f0,f292,f294,f307
  f294: extruded ~3.18x1.29mm, area 4.6mm2, adj f0,f293,f295,f307
  f295: extruded ~3.18x1.47mm, area 5mm2, adj f0,f294,f296,f307
  f296: extruded ~3.18x2mm, area 6.9mm2, adj f0,f295,f297,f307
  f297: plane 3.18x0.51mm, normal (-0.79,-0.61,0), area 2.1mm2, adj f0,f296,f298,f307
  f298: extruded ~3.18x0.82mm, area 3.1mm2, adj f0,f297,f299,f307
  f299: extruded ~3.18x0.78mm, area 2.5mm2, adj f0,f298,f300,f307
  f300: extruded ~3.18x0.89mm, area 3.1mm2, adj f0,f299,f301,f307
  f301: extruded ~3.18x0.84mm, area 2.9mm2, adj f0,f300,f302,f307
  f302: extruded ~3.18x0.7mm, area 2.3mm2, adj f0,f301,f303,f307
  f303: extruded ~3.18x0.67mm, area 2.5mm2, adj f0,f302,f304,f307
  f304: extruded ~3.18x1.15mm, area 5mm2, adj f0,f303,f305,f307
  f305: plane 3.18x1.75mm, normal (-0.71,0.71,0), area 7.9mm2, adj f0,f304,f306,f307
  f306: plane 3.18x0.65mm, normal (-1,0,0), area 2.1mm2, adj f0,f287,f305,f307
  f307: plane 6.73x4.36mm, normal (0,0,1), area 9.7mm2, adj f287,f288,f289,f290,f291,f292,f293,f294
  f308: plane 4.36x3.18mm, normal (0,-1,0), area 13.8mm2, adj f0,f309,f327,f328
  f309: plane 3.18x0.7mm, normal (1,0,0), area 2.2mm2, adj f0,f308,f310,f328
  f310: plane 3.41x3.18mm, normal (0,1,0), area 10.8mm2, adj f0,f309,f311,f328
  f311: plane 3.18x0.04mm, normal (1,0,0), area 0.1mm2, adj f0,f310,f312,f328
  f312: plane 3.18x1.45mm, normal (0.7,-0.71,0), area 6.4mm2, adj f0,f311,f313,f328
  f313: extruded ~3.18x1.56mm, area 6.5mm2, adj f0,f312,f314,f328
  f314: extruded ~3.18x1.25mm, area 4.2mm2, adj f0,f313,f315,f328
  f315: extruded ~3.18x1.29mm, area 4.6mm2, adj f0,f314,f316,f328
  f316: extruded ~3.18x1.47mm, area 5mm2, adj f0,f315,f317,f328
  f317: extruded ~3.18x2mm, area 6.9mm2, adj f0,f316,f318,f328
  f318: plane 3.18x0.51mm, normal (-0.79,-0.61,0), area 2.1mm2, adj f0,f317,f319,f328
  f319: extruded ~3.18x0.82mm, area 3.1mm2, adj f0,f318,f320,f328
  f320: extruded ~3.18x0.78mm, area 2.5mm2, adj f0,f319,f321,f328
  f321: extruded ~3.18x0.89mm, area 3.1mm2, adj f0,f320,f322,f328
  f322: extruded ~3.18x0.84mm, area 2.9mm2, adj f0,f321,f323,f328
  f323: extruded ~3.18x0.7mm, area 2.3mm2, adj f0,f322,f324,f328
  f324: extruded ~3.18x0.67mm, area 2.5mm2, adj f0,f323,f325,f328
  f325: extruded ~3.18x1.15mm, area 5mm2, adj f0,f324,f326,f328
  f326: plane 3.18x1.75mm, normal (-0.71,0.71,0), area 7.9mm2, adj f0,f325,f327,f328
  f327: plane 3.18x0.65mm, normal (-1,0,0), area 2.1mm2, adj f0,f308,f326,f328
  f328: plane 6.73x4.36mm, normal (0,0,1), area 9.7mm2, adj f308,f309,f310,f311,f312,f313,f314,f315
  f329: plane 108.46x5.33mm, normal (0,-1,0), area 578.5mm2, adj f0,f330,f332,f333
  f330: plane 10.03x5.33mm, normal (1,0,0), area 53.5mm2, adj f0,f329,f331,f333
  f331: plane 108.46x5.33mm, normal (0,1,0), area 578.5mm2, adj f0,f330,f332,f333
  f332: plane 10.03x5.33mm, normal (-1,0,0), area 53.5mm2, adj f0,f329,f331,f333
  f333: plane 108.46x10.03mm, normal (0,0,1), area 1088.2mm2, adj f329,f330,f331,f332
PLACE A t=(-13.26,26.88,-90.92)mm
PLACE B t=(-23.16,37.65,-95.11)mm
MATE planar A.f28 <-> B.f333  axis (0,0,-1) through (40.72,22.12,-90.92)mm
